# Revit family: TREF25K2A_TAC
name_source: partatom
category: Plumbing Fixtures
revit_build: Autodesk Revit 2018 (Build: 20170223_1515(x64)
units: mm (PartAtom-declared; Revit-internal decimal feet)

## family parameters
Always vertical = Yes
Cut with Voids When Loaded = No
OmniClass Number = 23.45.00.00
OmniClass Title = Sanitary, Laundry, and Cleaning Equipment
Part Type = Normal
Room Calculation Point = No
Round Connector Dimension = Use Diameter
Shared = No
Work Plane-Based = No

## types (1)
- TREF25K2A_TAC
    CW Connection = Yes
    Description = Conceald Toilet sensor Flush Valve
    Flow rate = 4.5LPF
    HW Connection = No
    Height = 185 mm
    Manufacturer = TOTO LTD.
    Material = Steel Use Stainless
    Model = TREF25K2A
    URL = https://asia.toto.com
    Vent Connection = No
    Voltage = DC
    Waste Connection = No
    Water Pressure = FP0.1～SP0.75MPa
    Width = 185 mm

## geometry (parser evidence)
native form markers: Sweep x2
no freeform markers — native parametric forms only
